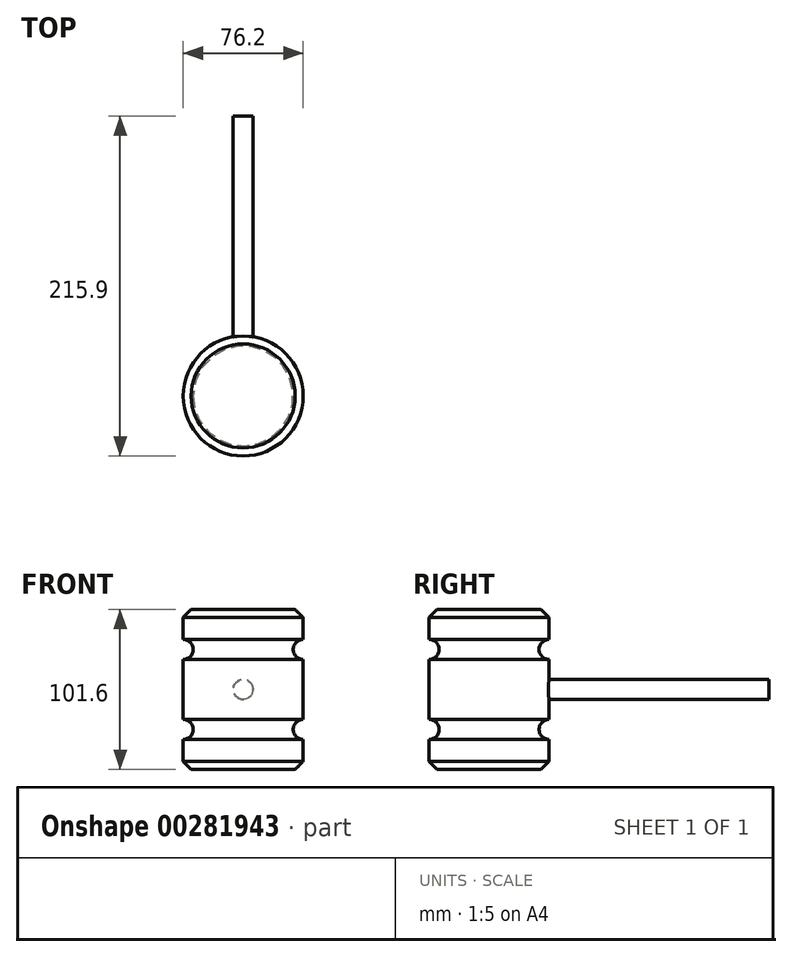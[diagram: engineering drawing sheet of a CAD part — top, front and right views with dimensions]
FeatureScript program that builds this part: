
annotation { "Feature Type Name" : "Feature", "Feature Type Description" : "" }
export const myFeature = defineFeature(function(context is Context, id is Id, definition is map)
    precondition{}
    {
        {
            var Q0;
            Q0=qCreatedBy(makeId("Front.planeOp"),FACE);
            var sketch = newSketch(context, id + "F0", { "sketchPlane" : qUnion([Q0])});
            skLineSegment(sketch, "E0.bottom", {"start": v(0, 0) * mm, "end": v(-38.1, 0) * mm});
            skLineSegment(sketch, "E0.top", {"start": v(0, 101.6) * mm, "end": v(-38.1, 101.6) * mm});
            skLineSegment(sketch, "E0.left", {"start": v(0, 0) * mm, "end": v(0, 25.4) * mm});
            skLineSegment(sketch, "E0.right", {"start": v(-38.1, 0) * mm, "end": v(-38.1, 101.6) * mm});
            skArc(sketch, "E1", {"start": v(0, 82.55) * mm, "mid": v(-6.35, 76.2) * mm, "end": v(0, 69.85) * mm});
            skArc(sketch, "E2", {"start": v(0, 31.75) * mm, "mid": v(-6.35, 25.4) * mm, "end": v(0, 19.05) * mm});
            skLineSegment(sketch, "E3.trimOffspring", {"start": v(0, 31.75) * mm, "end": v(0, 69.85) * mm});
            skLineSegment(sketch, "E4.trimOffspring", {"start": v(0, 76.2) * mm, "end": v(0, 101.6) * mm});
            skSolve(sketch);
        }
        {
            var Q0;
            Q0 = qSketchRegion(id + "F0", true);
            var Q1;
            Q1=sQuery(id+"F0.wireOp",EDGE,"E0.right");
            revolve(context, id + "F1", {"entities" : qUnion([Q0]), "axis" : qUnion([Q1]), "revolveType" : RevolveType.FULL});
        }
        {
            var Q0;
            Q0=makeQuery(id+"F1.opRevolve","SWEPT_FACE",FACE,{"disambiguationData":[OSD([sQuery(id+"F0.wireOp",EDGE,"E0.top")])]});
            var Q1;
            Q1=makeQuery(id+"F1.opRevolve","SWEPT_FACE",FACE,{"disambiguationData":[OSD([sQuery(id+"F0.wireOp",EDGE,"E0.bottom")])]});
            chamfer(context, id + "F2", {"entities" : qUnion([Q0, Q1]), "width" : 5.08 * mm, "tangentPropagation" : true});
        }
        {
            var Q0;
            Q0=qCreatedBy(makeId("Front.planeOp"),FACE);
            var sketch = newSketch(context, id + "F3", { "sketchPlane" : qUnion([Q0])});
            skCircle(sketch, "E5", {"center": v(-38.1, 50.8) * mm, "radius": 6.35 * mm});
            skSolve(sketch);
        }
        {
            var Q0;
            Q0 = qSketchRegion(id + "F3", true);
            extrude(context, id + "F4", {"entities" : qUnion([Q0]), "operationType" : NewBodyOperationType.REMOVE, "oppositeDirection" : true, "depth" : 127 * mm});
        }
        {
            var Q0;
            Q0=makeQuery(id+"F4.boolean.opBoolean","COPY",FACE,{"derivedFrom":makeQuery(id+"F4.opExtrude","CAP_FACE",FACE,{"disambiguationData":[OSD([sQuery(id+"F3.wireOp",EDGE,"E5")])],"isStart":true})});
            extrude(context, id + "F5", {"entities" : qUnion([Q0]), "operationType" : NewBodyOperationType.ADD, "depth" : 177.8 * mm});
        }
    });
